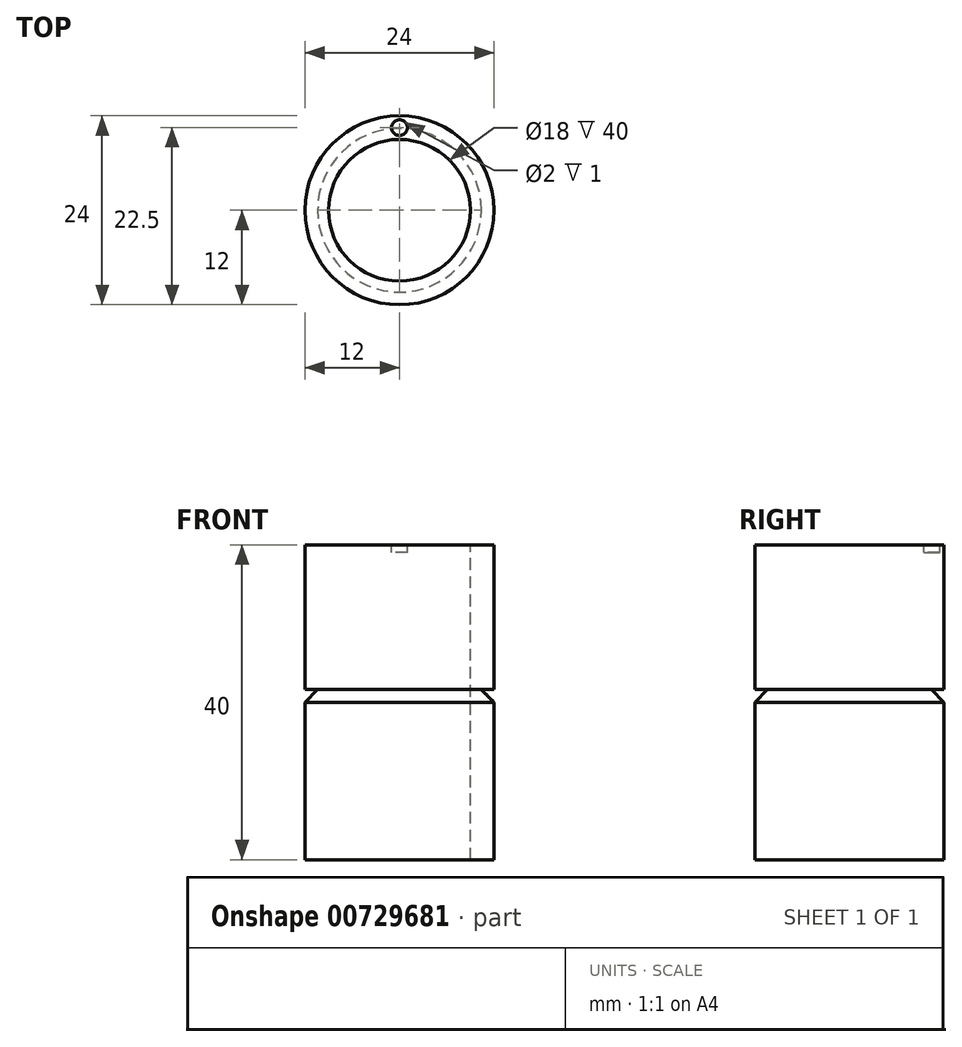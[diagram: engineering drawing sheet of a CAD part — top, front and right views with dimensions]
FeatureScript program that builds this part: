
annotation { "Feature Type Name" : "Feature", "Feature Type Description" : "" }
export const myFeature = defineFeature(function(context is Context, id is Id, definition is map)
    precondition{}
    {
        {
            var Q0;
            Q0=qCreatedBy(makeId("Top.planeOp"),FACE);
            var sketch = newSketch(context, id + "F0", { "sketchPlane" : qUnion([Q0])});
            skCircle(sketch, "E0", {"center": v(0, 0) * mm, "radius": 12 * mm});
            skSolve(sketch);
        }
        {
            var Q0;
            Q0 = qSketchRegion(id + "F0", true);
            extrude(context, id + "F1", {"entities" : qUnion([Q0]), "depth" : 40 * mm, "offsetDistance" : 25 * mm});
        }
        {
            var Q0;
            Q0=makeQuery(id+"F1.opExtrude","CAP_FACE",FACE,{"disambiguationData":[OSD([sQuery(id+"F0.wireOp",EDGE,"E0")])],"isStart":false});
            var sketch = newSketch(context, id + "F2", { "sketchPlane" : qUnion([Q0])});
            skCircle(sketch, "E1", {"center": v(0, 0) * mm, "radius": 9 * mm});
            skSolve(sketch);
        }
        {
            var Q0;
            Q0=makeQuery(id+"F2.imprint","IMPRINT",FACE,{"disambiguationData":[TD([[makeQuery(id+"F2.imprint","IMPRINT",EDGE,{"derivedFrom":sQuery(id+"F2.wireOp",EDGE,"E1")}),1.0]])]});
            extrude(context, id + "F3", {"entities" : qUnion([Q0]), "operationType" : NewBodyOperationType.REMOVE, "endBound" : BoundingType.THROUGH_ALL, "oppositeDirection" : true, "depth" : 25 * mm, "offsetDistance" : 25 * mm});
        }
        {
            var Q0;
            Q0=qCreatedBy(makeId("Front.planeOp"),FACE);
            var sketch = newSketch(context, id + "F4", { "sketchPlane" : qUnion([Q0])});
            skLineSegment(sketch, "E2", {"start": v(-12, 20) * mm, "end": v(-10.4, 21.6) * mm});
            skLineSegment(sketch, "E3", {"start": v(-10.4, 21.6) * mm, "end": v(-12, 21.6) * mm});
            skLineSegment(sketch, "E4", {"start": v(-12, 21.6) * mm, "end": v(-12, 20) * mm});
            skSolve(sketch);
        }
        {
            var Q0;
            Q0=qCreatedBy(makeId("Front.planeOp"),FACE);
            var sketch = newSketch(context, id + "F5", { "sketchPlane" : qUnion([Q0])});
            skLineSegment(sketch, "E5", {"start": v(0, 0) * mm, "end": v(0, 41.27) * mm, "construction": true});
            skSolve(sketch);
        }
        {
            var Q0;
            Q0 = qSketchRegion(id + "F4", true);
            var Q1;
            Q1=sQuery(id+"F5.wireOp",EDGE,"E5");
            revolve(context, id + "F6", {"operationType" : NewBodyOperationType.REMOVE, "surfaceOperationType" : NewSurfaceOperationType.NEW, "entities" : qUnion([Q0]), "axis" : qUnion([Q1]), "revolveType" : RevolveType.FULL, "oppositeDirection" : true});
        }
        {
            var Q0;
            Q0=makeQuery(id+"F1.opExtrude","CAP_FACE",FACE,{"disambiguationData":[OSD([sQuery(id+"F0.wireOp",EDGE,"E0")])],"isStart":false});
            var sketch = newSketch(context, id + "F7", { "sketchPlane" : qUnion([Q0])});
            skCircle(sketch, "E6", {"center": v(0, 10.5) * mm, "radius": 1 * mm});
            skSolve(sketch);
        }
        {
            var Q0;
            Q0 = qSketchRegion(id + "F7", true);
            extrude(context, id + "F8", {"entities" : qUnion([Q0]), "operationType" : NewBodyOperationType.REMOVE, "oppositeDirection" : true, "depth" : 1 * mm, "offsetDistance" : 25 * mm});
        }
    });
